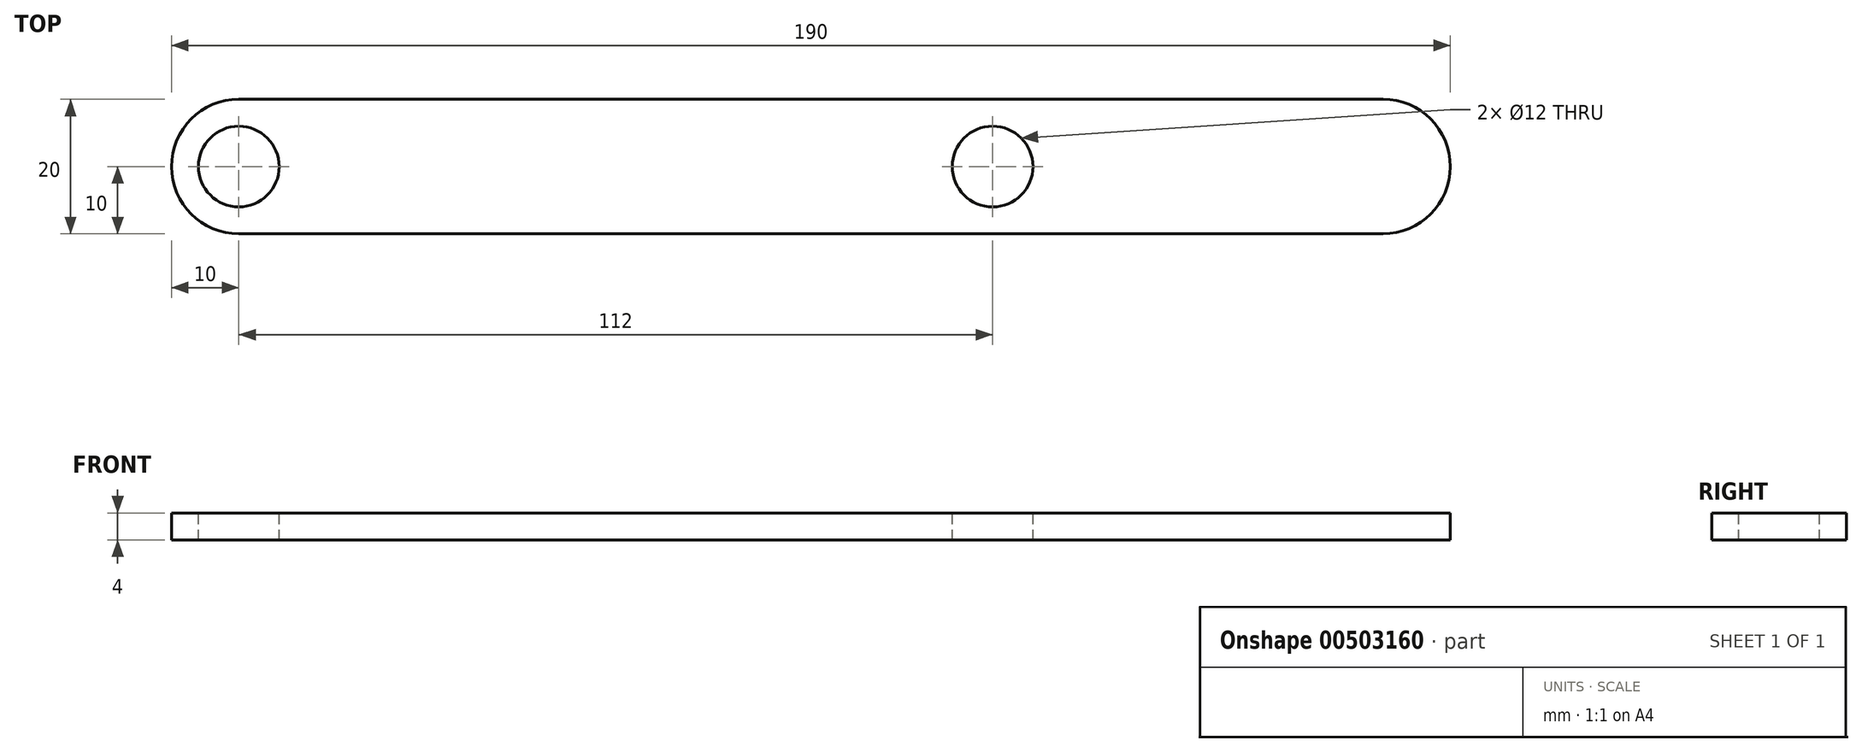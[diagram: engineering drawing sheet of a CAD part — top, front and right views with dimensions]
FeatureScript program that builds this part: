
annotation { "Feature Type Name" : "Feature", "Feature Type Description" : "" }
export const myFeature = defineFeature(function(context is Context, id is Id, definition is map)
    precondition{}
    {
        {
            var Q0;
            Q0=qCreatedBy(makeId("Top.planeOp"),FACE);
            var sketch = newSketch(context, id + "F0", { "sketchPlane" : qUnion([Q0])});
            skLineSegment(sketch, "E0.bottom", {"start": v(95, 10) * mm, "end": v(-95, 10) * mm});
            skLineSegment(sketch, "E0.top", {"start": v(95, -10) * mm, "end": v(-95, -10) * mm});
            skLineSegment(sketch, "E0.left", {"start": v(95, 10) * mm, "end": v(95, -10) * mm});
            skLineSegment(sketch, "E0.right", {"start": v(-95, 10) * mm, "end": v(-95, -10) * mm});
            skPoint(sketch, "E0.middle", {"position": v(0, 0) * mm});
            skSolve(sketch);
        }
        {
            var Q0;
            Q0=makeQuery(id+"F0.imprint","IMPRINT",FACE,{"disambiguationData":[TD([[makeQuery(id+"F0.imprint","IMPRINT",EDGE,{"derivedFrom":sQuery(id+"F0.wireOp",EDGE,"E0.bottom")}),1.0]])]});
            extrude(context, id + "F1", {"entities" : qUnion([Q0]), "depth" : 4 * mm});
        }
        {
            var Q0;
            Q0=makeQuery(id+"F1.opExtrude","CAP_FACE",FACE,{"disambiguationData":[OSD([sQuery(id+"F0.wireOp",EDGE,"E0.bottom"),sQuery(id+"F0.wireOp",EDGE,"E0.top"),sQuery(id+"F0.wireOp",EDGE,"E0.left"),sQuery(id+"F0.wireOp",EDGE,"E0.right")])],"isStart":false});
            var sketch = newSketch(context, id + "F2", { "sketchPlane" : qUnion([Q0])});
            skLineSegment(sketch, "E1", {"start": v(-95, 0) * mm, "end": v(-85, 0) * mm, "construction": true});
            skPoint(sketch, "E1.endSnap0", {"position": v(-95, 0) * mm});
            skLineSegment(sketch, "E2", {"start": v(95, 0) * mm, "end": v(85, 0) * mm, "construction": true});
            skPoint(sketch, "E2.endSnap0", {"position": v(95, 0) * mm});
            skCircle(sketch, "E3", {"center": v(-85, 0) * mm, "radius": 6 * mm});
            skLineSegment(sketch, "E4", {"start": v(-95, 0) * mm, "end": v(27, 0) * mm, "construction": true});
            skCircle(sketch, "E5", {"center": v(27, 0) * mm, "radius": 6 * mm});
            skSolve(sketch);
        }
        {
            var Q0;
            Q0=makeQuery(id+"F2.imprint","IMPRINT",FACE,{"disambiguationData":[TD([[makeQuery(id+"F2.imprint","IMPRINT",EDGE,{"derivedFrom":sQuery(id+"F2.wireOp",EDGE,"E3")}),1.0]])]});
            var Q1;
            Q1=makeQuery(id+"F2.imprint","IMPRINT",FACE,{"disambiguationData":[TD([[makeQuery(id+"F2.imprint","IMPRINT",EDGE,{"derivedFrom":sQuery(id+"F2.wireOp",EDGE,"E5")}),1.0]])]});
            extrude(context, id + "F3", {"entities" : qUnion([Q0, Q1]), "operationType" : NewBodyOperationType.REMOVE, "endBound" : BoundingType.THROUGH_ALL, "oppositeDirection" : true, "depth" : 25 * mm});
        }
        {
            var Q0;
            Q0=makeQuery(id+"F1.opExtrude","SWEPT_EDGE",EDGE,{"disambiguationData":[OSD([sQuery(id+"F0.wireOp",EDGE,"E0.top"),sQuery(id+"F0.wireOp",EDGE,"E0.right")])]});
            var Q1;
            Q1=makeQuery(id+"F1.opExtrude","SWEPT_EDGE",EDGE,{"disambiguationData":[OSD([sQuery(id+"F0.wireOp",EDGE,"E0.bottom"),sQuery(id+"F0.wireOp",EDGE,"E0.right")])]});
            var Q2;
            Q2=makeQuery(id+"F1.opExtrude","SWEPT_EDGE",EDGE,{"disambiguationData":[OSD([sQuery(id+"F0.wireOp",EDGE,"E0.bottom"),sQuery(id+"F0.wireOp",EDGE,"E0.left")])]});
            var Q3;
            Q3=makeQuery(id+"F1.opExtrude","SWEPT_EDGE",EDGE,{"disambiguationData":[OSD([sQuery(id+"F0.wireOp",EDGE,"E0.top"),sQuery(id+"F0.wireOp",EDGE,"E0.left")])]});
            fillet(context, id + "F4", {"entities" : qUnion([Q0, Q1, Q2, Q3]), "radius" : 10 * mm, "tangentPropagation" : true, "allowEdgeOverflow" : false});
        }
    });
